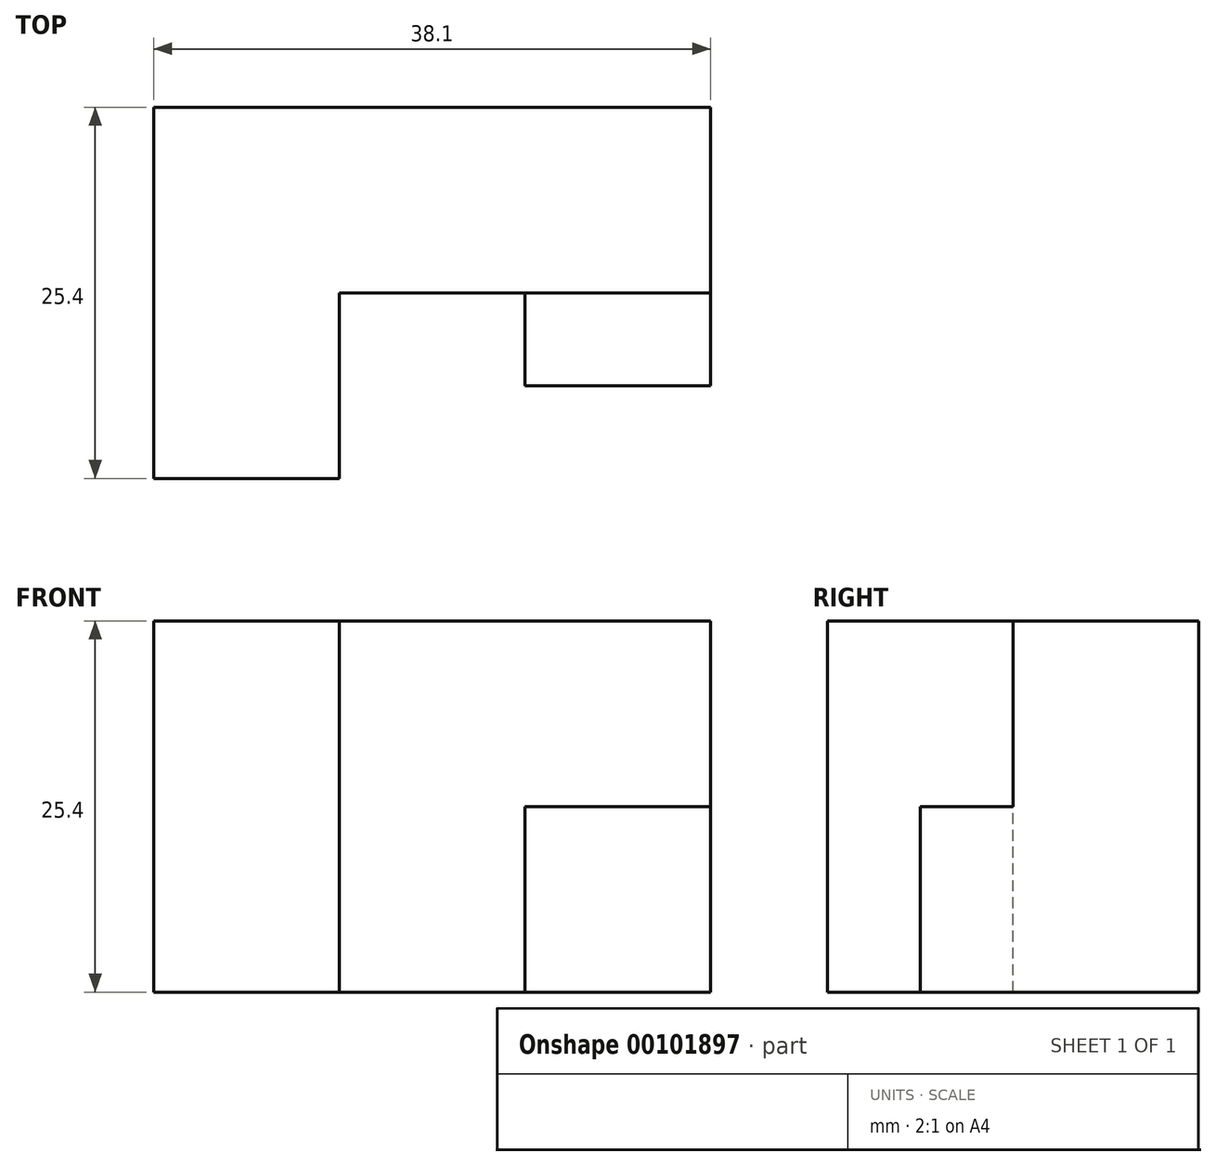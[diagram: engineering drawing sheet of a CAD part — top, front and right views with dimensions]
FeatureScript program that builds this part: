
annotation { "Feature Type Name" : "Feature", "Feature Type Description" : "" }
export const myFeature = defineFeature(function(context is Context, id is Id, definition is map)
    precondition{}
    {
        {
            var Q0;
            Q0=qCreatedBy(makeId("Top.planeOp"),FACE);
            var sketch = newSketch(context, id + "F0", { "sketchPlane" : qUnion([Q0])});
            skLineSegment(sketch, "E0", {"start": v(0, 0) * mm, "end": v(0, 25.4) * mm});
            skLineSegment(sketch, "E1", {"start": v(0, 25.4) * mm, "end": v(38.1, 25.4) * mm});
            skLineSegment(sketch, "E2", {"start": v(38.1, 12.7) * mm, "end": v(12.7, 12.7) * mm});
            skLineSegment(sketch, "E3", {"start": v(12.7, 12.7) * mm, "end": v(12.7, 0) * mm});
            skLineSegment(sketch, "E4", {"start": v(12.7, 0) * mm, "end": v(0, 0) * mm});
            skLineSegment(sketch, "E5", {"start": v(38.1, 25.4) * mm, "end": v(38.1, 12.7) * mm});
            skSolve(sketch);
        }
        {
            var Q0;
            Q0=makeQuery(id+"F0.imprint","IMPRINT",FACE,{"disambiguationData":[TD([[makeQuery(id+"F0.imprint","IMPRINT",EDGE,{"derivedFrom":sQuery(id+"F0.wireOp",EDGE,"E0")}),-1.0]])]});
            extrude(context, id + "F1", {"entities" : qUnion([Q0]), "depth" : 25.4 * mm});
        }
        {
            var Q0;
            Q0=qCreatedBy(makeId("Front.planeOp"),FACE);
            var sketch = newSketch(context, id + "F2", { "sketchPlane" : qUnion([Q0])});
            skLineSegment(sketch, "E6.bottom", {"start": v(25.4, 0) * mm, "end": v(38.1, 0) * mm});
            skLineSegment(sketch, "E6.top", {"start": v(25.4, 12.7) * mm, "end": v(38.1, 12.7) * mm});
            skLineSegment(sketch, "E6.left", {"start": v(25.4, 0) * mm, "end": v(25.4, 12.7) * mm});
            skLineSegment(sketch, "E6.right", {"start": v(38.1, 0) * mm, "end": v(38.1, 12.7) * mm});
            skSolve(sketch);
        }
        {
            var Q0;
            Q0 = qSketchRegion(id + "F2", true);
            extrude(context, id + "F3", {"entities" : qUnion([Q0]), "operationType" : NewBodyOperationType.ADD, "oppositeDirection" : true, "depth" : 12.7 * mm});
        }
        {
            var Q0;
            Q0=qCreatedBy(makeId("Top.planeOp"),FACE);
            var sketch = newSketch(context, id + "F4", { "sketchPlane" : qUnion([Q0])});
            skLineSegment(sketch, "E7.bottom", {"start": v(25.4, 0) * mm, "end": v(38.1, 0) * mm});
            skLineSegment(sketch, "E7.top", {"start": v(25.4, 0) * mm, "end": v(38.1, 0) * mm});
            skLineSegment(sketch, "E7.left", {"start": v(25.4, 0) * mm, "end": v(25.4, 0) * mm});
            skLineSegment(sketch, "E7.right", {"start": v(38.1, 0) * mm, "end": v(38.1, 0) * mm});
            skLineSegment(sketch, "E8.bottom", {"start": v(38.1, 6.35) * mm, "end": v(25.4, 6.35) * mm});
            skLineSegment(sketch, "E8.top", {"start": v(38.1, 0) * mm, "end": v(25.4, 0) * mm});
            skLineSegment(sketch, "E8.left", {"start": v(38.1, 6.35) * mm, "end": v(38.1, 0) * mm});
            skLineSegment(sketch, "E8.right", {"start": v(25.4, 6.35) * mm, "end": v(25.4, 0) * mm});
            skSolve(sketch);
        }
        {
            var Q0;
            Q0 = qSketchRegion(id + "F4", true);
            extrude(context, id + "F5", {"entities" : qUnion([Q0]), "operationType" : NewBodyOperationType.REMOVE, "depth" : 12.7 * mm});
        }
    });
